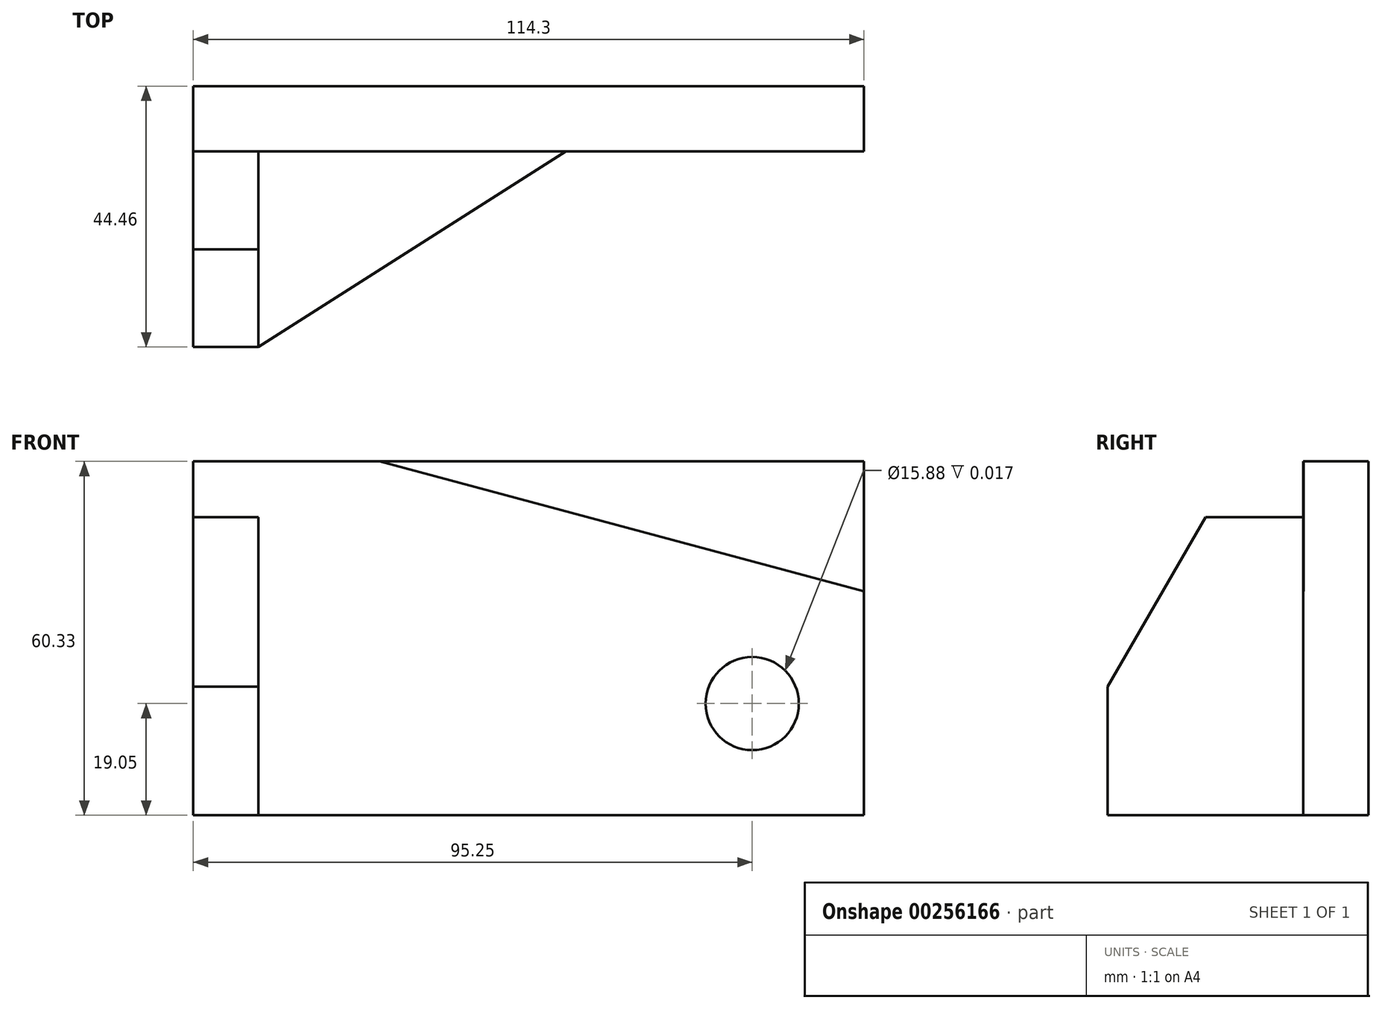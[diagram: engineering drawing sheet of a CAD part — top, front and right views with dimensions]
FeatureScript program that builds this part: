
annotation { "Feature Type Name" : "Feature", "Feature Type Description" : "" }
export const myFeature = defineFeature(function(context is Context, id is Id, definition is map)
    precondition{}
    {
        {
            var Q0;
            Q0=qCreatedBy(makeId("Top.planeOp"),FACE);
            var sketch = newSketch(context, id + "F0", { "sketchPlane" : qUnion([Q0])});
            skLineSegment(sketch, "E0.bottom", {"start": v(-46.04, -22.23) * mm, "end": v(-57.15, -22.23) * mm});
            skLineSegment(sketch, "E0.top", {"start": v(57.15, 22.23) * mm, "end": v(-57.15, 22.22) * mm});
            skLineSegment(sketch, "E0.left", {"start": v(57.15, 11.11) * mm, "end": v(57.15, 22.23) * mm});
            skLineSegment(sketch, "E0.right", {"start": v(-57.15, -22.23) * mm, "end": v(-57.15, 22.22) * mm});
            skPoint(sketch, "E0.middle", {"position": v(0, 0) * mm});
            skLineSegment(sketch, "E1", {"start": v(-46.04, 11.11) * mm, "end": v(-46.04, -22.23) * mm});
            skLineSegment(sketch, "E2", {"start": v(-57.15, 11.11) * mm, "end": v(57.15, 11.11) * mm});
            skLineSegment(sketch, "E3", {"start": v(-46.04, -22.23) * mm, "end": v(6.35, 11.11) * mm});
            skLineSegment(sketch, "E4", {"start": v(-25.4, 22.23) * mm, "end": v(-25.4, 11.11) * mm});
            skPoint(sketch, "E5.orphan", {"position": v(6.35, 22.23) * mm});
            skPoint(sketch, "E6.start.orphan", {"position": v(-57.15, -11.11) * mm});
            skPoint(sketch, "E7.orphan", {"position": v(57.15, -22.22) * mm});
            skSolve(sketch);
        }
        {
            var Q0;
            {var subQ0=sQuery(id+"F0.wireOp",EDGE,"E1");Q0=makeQuery(id+"F0.imprint","IMPRINT",FACE,{"disambiguationData":[TD([[makeQuery(id+"F0.imprint","IMPRINT",EDGE,{"derivedFrom":subQ0}),1.0]])]});}
            extrude(context, id + "F1", {"entities" : qUnion([Q0]), "depth" : 7 / 406.4 * mm});
        }
        {
            var Q0;
            {var subQ2=sQuery(id+"F0.wireOp",EDGE,"E4");Q0=makeQuery(id+"F0.imprint","IMPRINT",FACE,{"disambiguationData":[TD([[makeQuery(id+"F0.imprint","IMPRINT",EDGE,{"derivedFrom":subQ2}),-1.0]])]});}
            var Q1;
            {var subQ1=sQuery(id+"F0.wireOp",EDGE,"E0.left");Q1=makeQuery(id+"F0.imprint","IMPRINT",FACE,{"disambiguationData":[TD([[makeQuery(id+"F0.imprint","IMPRINT",EDGE,{"derivedFrom":subQ1}),1.0]])]});}
            extrude(context, id + "F2", {"entities" : qUnion([Q0, Q1]), "operationType" : NewBodyOperationType.ADD, "depth" : 60.32 * mm});
        }
        {
            var Q0;
            {var subQ0=sQuery(id+"F0.wireOp",EDGE,"E0.bottom");Q0=makeQuery(id+"F0.imprint","IMPRINT",FACE,{"disambiguationData":[TD([[makeQuery(id+"F0.imprint","IMPRINT",EDGE,{"derivedFrom":subQ0}),-1.0]])]});}
            extrude(context, id + "F3", {"entities" : qUnion([Q0]), "operationType" : NewBodyOperationType.ADD, "depth" : 50.8 * mm});
        }
        {
            var Q0;
            Q0=makeQuery(id+"F2.opExtrude","SWEPT_FACE",FACE,{"disambiguationData":[OSD([sQuery(id+"F0.wireOp",EDGE,"E2")])]});
            var sketch = newSketch(context, id + "F4", { "sketchPlane" : qUnion([Q0])});
            skLineSegment(sketch, "E8", {"start": v(-25.4, 60.33) * mm, "end": v(57.15, 38.2) * mm});
            skPoint(sketch, "E9.end.orphan", {"position": v(-25.4, 0) * mm});
            skCircle(sketch, "E10", {"center": v(38.1, 19.05) * mm, "radius": 7.94 * mm});
            skPoint(sketch, "E11.orphan", {"position": v(38.1, 0) * mm});
            skPoint(sketch, "E12.orphan", {"position": v(57.15, 19.05) * mm});
            skSolve(sketch);
        }
        {
            var Q0;
            Q0=makeQuery(id+"F3.opExtrude","SWEPT_FACE",FACE,{"disambiguationData":[OSD([sQuery(id+"F0.wireOp",EDGE,"E1")])]});
            var sketch = newSketch(context, id + "F5", { "sketchPlane" : qUnion([Q0])});
            skLineSegment(sketch, "E13", {"start": v(-22.23, 21.93) * mm, "end": v(-5.56, 50.8) * mm});
            skSolve(sketch);
        }
        {
            var Q0;
            {var subQ0=sQuery(id+"F5.wireOp",EDGE,"E13");Q0=makeQuery(id+"F5.imprint","IMPRINT",FACE,{"disambiguationData":[TD([[makeQuery(id+"F5.imprint","IMPRINT",EDGE,{"derivedFrom":subQ0}),1.0]])]});}
            extrude(context, id + "F6", {"entities" : qUnion([Q0]), "operationType" : NewBodyOperationType.REMOVE, "oppositeDirection" : true, "depth" : 11.1 * mm});
        }
        {
            var Q0;
            {var subQ0=sQuery(id+"F4.wireOp",EDGE,"E8");Q0=makeQuery(id+"F4.imprint","IMPRINT",FACE,{"disambiguationData":[TD([[makeQuery(id+"F4.imprint","IMPRINT",EDGE,{"derivedFrom":subQ0}),1.0]])]});}
            extrude(context, id + "F7", {"entities" : qUnion([Q0]), "operationType" : NewBodyOperationType.REMOVE, "oppositeDirection" : true, "depth" : 7 / 406.4 * mm});
        }
        {
            var Q0;
            Q0=makeQuery(id+"F4.imprint","IMPRINT",FACE,{"disambiguationData":[TD([[makeQuery(id+"F4.imprint","IMPRINT",EDGE,{"derivedFrom":sQuery(id+"F4.wireOp",EDGE,"E10")}),1.0]])]});
            extrude(context, id + "F8", {"entities" : qUnion([Q0]), "operationType" : NewBodyOperationType.REMOVE, "oppositeDirection" : true, "depth" : 7 / 406.4 * mm});
        }
    });
